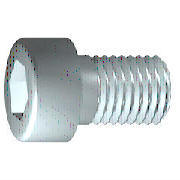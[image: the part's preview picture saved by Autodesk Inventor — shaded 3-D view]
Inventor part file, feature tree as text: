
AUTODESK INVENTOR PART (.ipt)
format: ipt  version: 2013 (Build 170138000, 138)  size: 182,784 bytes
history: native  units: mm (DEFAULTED — no unit token found)
features: sketch x2, extrude x1, plane x1
ambient origin geometry x7: Origin, YZ Plane, XY Plane, X Axis, Y Axis, Z Axis, Center Point
bodies: Solid1 (feature_tree), Body (feature_tree)
feature tree (4):
  extrude  "Slot"  Depth=3.1751mm
  plane  "Work Plane1"
  sketch  "Sketch1"  dims[d1=31.75mm d2=3.1751mm]
  sketch  "Sketch2"  dims[d3=6.35mm d4=3.048mm d5=60.0deg d6=6.35mm d7=6.35mm d8=5.513926mm d9=9.525mm d10=90.0deg d11=10.0mm d12=0.0mm d13=31.75mm d14=0.0mm d15=0.75565mm d16=0.75565mm d17=0.635mm d19=0.0mm d26=50.8mm d27=45.0deg d28=0.0mm d29=0.0mm]
